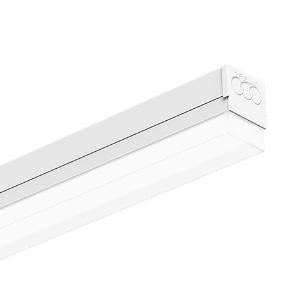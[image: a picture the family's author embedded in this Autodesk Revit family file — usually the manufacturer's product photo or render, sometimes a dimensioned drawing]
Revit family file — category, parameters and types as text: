
# Revit family: 3f_filippi_-_3f_zeta_dr_3f_filippi_-_10984_-_3f_zeta_dr_1x22_led_ep_l1489
name_source: partatom
category: Lighting Fixtures
units: mm (PartAtom-declared; Revit-internal decimal feet)

## family parameters
Cut with Voids When Loaded = No
Host = Face
Light Source = No
Part Type = Normal
Room Calculation Point = No
Round Connector Dimension = Use Diameter
Shared = No

## types (1)
- 3F Filippi - 3F Zeta DR (1 x LED, 3126 lm, 25.5 W, 4000 K)
    Apparent Load = 26 VA
    Approval mark = ENEC
    CIE Flux Codes = 41 72 91 86 100
    Color Rendering = 80
    Color Temperature = 4000 K
    Control Gear = Electronic ballast
    Default Elevation = 1800 mm
    Description = ILLUMINOTECHNICAL
Luminous efficiency 100% (DLOR 86%, ULOR 14%).
Initial luminous flux of the luminaire 3126 lm.
Emergency luminaire luminous flux BLF 15.2%.
Diffused symmetric distribution.
Installation Interdistance Transv.D = 1.31 x hu - Long.D = 1.25 x hu.
Tabular UGR (CIE 117 - 4H-8H; S=0.25H; 70/50/20): RUG 23.3 - 21.8.
Beam angle: 136° - 112°.
Luminous efficacy 123 lm/W.
Lifetime (L93/B10): 30000 h. (tq+25°C)
Lifetime (L90/B10): 50000 h. (tq+25°C)
Lifetime (L85/B10): 80000 h. (tq+25°C)
Lifetime (L80/B10): 100000 h. (tq+25°C)
Sudden decreased luminous flux after 50000 hours: 0% (C0).
Photobiological safety in compliance with IEC/TR 62778: RG0 risk exempt, (IEC 62471).
In compliance with IEC/EN 62722-2-1 - IEC/EN 62717 standards.

SOURCE
Linear LED module 22W/840.
Energy efficiency class (UE 2019/2020 - UE 2019/2015): D.
CIE 13.3 Colour rendering index: CRI >80 (R9 <50%).
IES TM-30 Fidelity Index: Rf = 84 Rg = 95.
CCT nominal colour temperature 4000 K.
Colour initial tolerance (MacAdam): SDCM 3.

MECHANICAL
Housing in hot-galvanised steel, painted in white polyester, obtained through rolling process.
Light unit in hot-galvanised steel, painted in white polyester base with fixing springs and retractable safety hooks in stainless steel.
Rectangular screen in self-extinguishing polycarbonate, UV stabilised, opal, with smooth outer surface.
End caps in white polycarbonate.
Pair of stainless steel sliding brackets with sliding block screws.
Luminaire with limited surface temperature. - D - (EN 60598-2-24)
Dimensions: 1489x62 mm, height 81 mm. Weight 4.56 kg.
IP40 protection degree.
Mechanical strength to impacts IK06 (1 joule).
Glow-wire test resistance 850°C.

ELECTRICAL
Halogen Free electronic wiring 230V-50/60Hz, power factor 0.85, THD <25%, constant output current, SELV, class I, 1 driver.
Power of the luminaire 25.5 W.
CE - IEC 60598-1 - EN 60598-1.
EP maintained emergency wiring on board, 1h duration, 24h recharge; compliant with EN 60598-2-22, excluding high risk areas.
SAFE FLICKER: PstLM=<1 and SVM=<0.4 (IEC TR 61547-1 and IEC TR 63158), to ensure a more comfortable and safe light.
Ambient temperature from +5°C to +25°C.
Temperature class T6 max 85°C.
Relative humidity UR: <85%.

INSTALLATION
Ceiling / Suspended / Wall.
All accessories dedicated to this product are available on the Catalog and on our website www.3F-Filippi.com.

APPLICATIONS
Suitable product for food production plants (HACCP), IFS (Food Version 6), BRC (GSFS Food Version 7).
In commercial environments, exhibition areas, shops and stores.

WARNING
Luminaire designed for disposal/recycling at end-of-life.
Replaceable (LED only) light source by a professional. Replaceable control gear by a professional.
    Height = 81 mm
    Lamp = 1 x LED
    Lamp Light Flux = 3126 lm
    Lamp Power = 25.5 W
    Lamp count = 1
    Length = 1489 mm
    Lifetime = 50000 h
    Luminous efficacy = 123 lm/W
    Manufacturer = 3F Filippi
    ModVariant = No
    Model = 3F Filippi - 10984 - 3F Zeta DR 1x22 LED EP L1489
    Mounting Place = Ceiling
    Mounting Type = Pendant
    Number of Poles = 1
    OnlyDefault = Yes
    Power Factor = 1
    Product Name = 3F Filippi - 3F Zeta DR
    Product group = pendant luminaire
    ProductGroupID = 9
    Protection Class = Protection class I
    Protection Degree = IP 40
    RLX_Detail_Level = 1
    RLX_Emergency_Light_Flux = 0 lm
    RLX_Emergency_Type = 0
    RLX_Emergency_Type_DB = No
    RlxData = <blob elided: 32701 chars, md5=8978f56c>
    Socket = socket
    Standby Power = 0 W
    System Light Flux = 3126 lm
    System Power = 26 W
    Type Comments = Product without accessories
    Type Image = 3ffilippi_3f_zeta_dr.jpg
    URL = http://relux.com
    VarID = ---
    Voltage = 0 V
    Weight = 0.00 kg
    Width = 62 mm  [stored 0.203412 ft]

note: [stored X ft] marks values corroborated as IEEE doubles in the binary element streams (Revit-internal decimal feet)

## geometry (parser evidence)
native form markers: Blend x4, Sweep x15
no freeform markers — native parametric forms only
